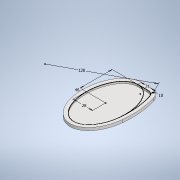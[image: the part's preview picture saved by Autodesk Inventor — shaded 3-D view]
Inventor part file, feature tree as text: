
AUTODESK INVENTOR PART (.ipt)
format: ipt  version: 2022 (Build 260153070, 153G)  size: 268,800 bytes
history: native  units: mm
features: extrude x4, sketch x3, thicken_offset x3, projected_geometry x2
ambient origin geometry x8: Origin, YZ Plane, XZ Plane, XY Plane, X Axis, Y Axis, Z Axis, Center Point
bodies: Solid1 (feature_tree), Solid3 (feature_tree), Solid4 (feature_tree), Solid5 (feature_tree)
feature tree (12):
  sketch  "Sketch1"  dims[d0=28.0mm d1=46.0mm]
  extrude  "Extrusion1"  Depth=46.0mm
  thicken_offset  "Thicken3"
  thicken_offset  "Thicken4"
  sketch  "Sketch3"  dims[d3=120.0mm d5=21.0mm]
  extrude  "Extrusion6"  Depth=21.0mm
  extrude  "Extrusion7"  Depth=2.0mm TaperAngle=0.0deg
  thicken_offset  "Thicken6"
  extrude  "Extrusion8"  Depth=2.0mm
  projected_geometry  "Projected Loop2"
  sketch  "Sketch4"  dims[d6=10.0mm d7=2.0mm d8=0.0mm d19=2.0mm d20=3.0mm d23=5.0mm d24=2.0mm d25=3.0mm d26=6.0mm d27=0.0mm d28=0.0mm d29=2.0mm d30=0.0mm d33=3.0mm d34=3.0mm d35=5.0mm d36=0.0mm]
  projected_geometry  "Projected Loop3"
